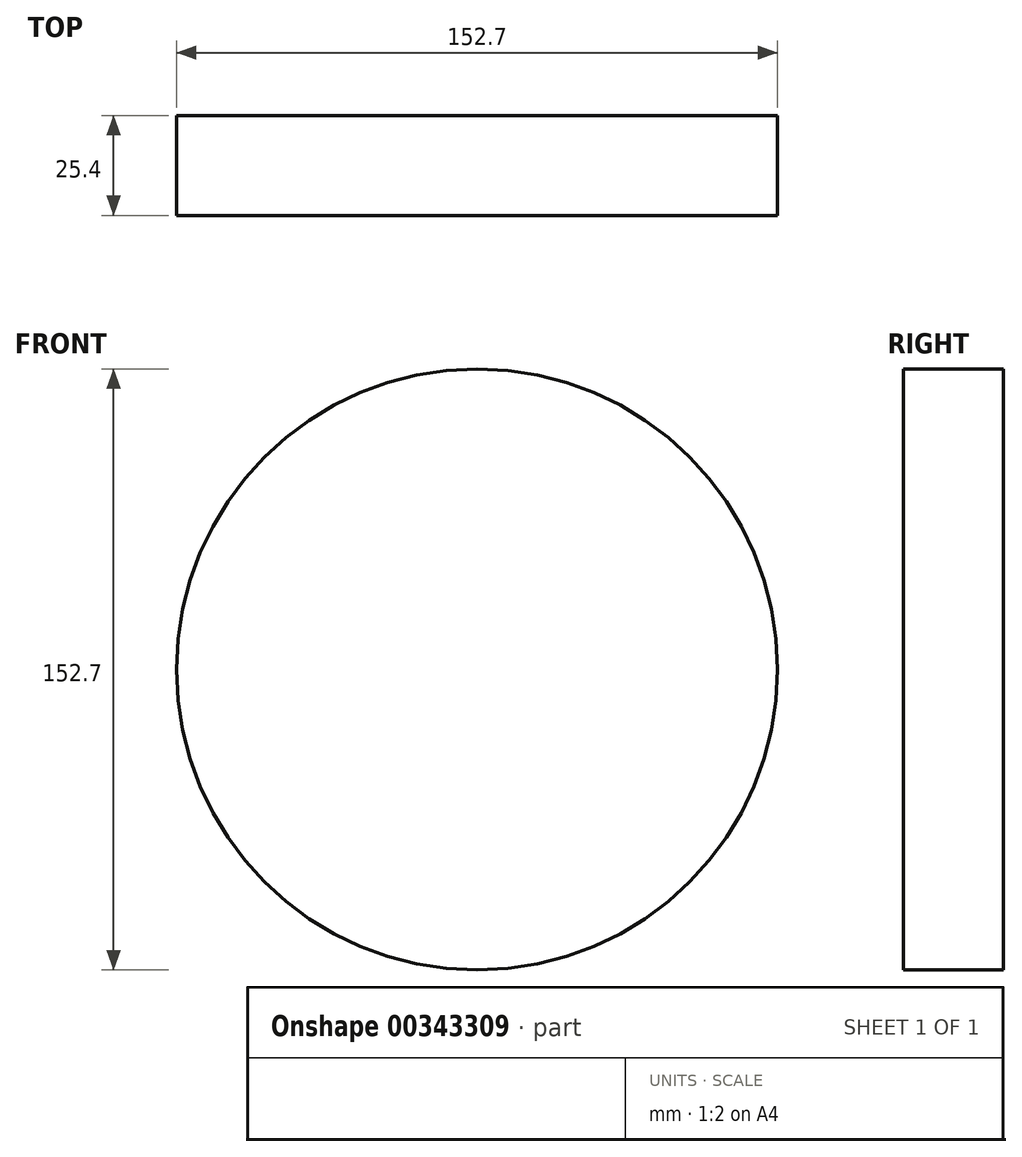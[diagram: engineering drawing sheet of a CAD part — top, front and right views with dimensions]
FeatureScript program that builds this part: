
annotation { "Feature Type Name" : "Feature", "Feature Type Description" : "" }
export const myFeature = defineFeature(function(context is Context, id is Id, definition is map)
    precondition{}
    {
        {
            var Q0;
            Q0=qCreatedBy(makeId("Front.planeOp"),FACE);
            var sketch = newSketch(context, id + "F0", { "sketchPlane" : qUnion([Q0])});
            skCircle(sketch, "E0", {"center": v(0, 0) * mm, "radius": 76.35 * mm});
            skSolve(sketch);
        }
        {
            var Q0;
            Q0=makeQuery(id+"F0.imprint","IMPRINT",FACE,{"disambiguationData":[TD([[makeQuery(id+"F0.imprint","IMPRINT",EDGE,{"derivedFrom":sQuery(id+"F0.wireOp",EDGE,"E0")}),1.0]])]});
            extrude(context, id + "F1", {"entities" : qUnion([Q0]), "depth" : 25.4 * mm});
        }
    });
